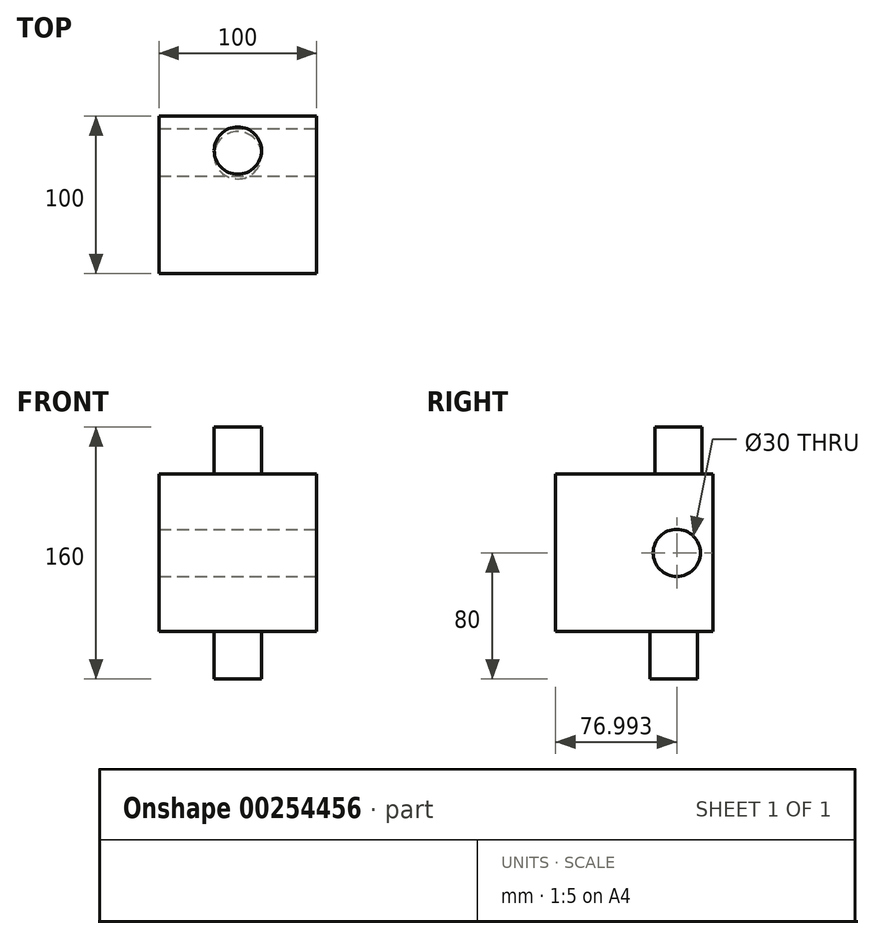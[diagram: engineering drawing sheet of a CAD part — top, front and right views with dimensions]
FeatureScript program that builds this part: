
annotation { "Feature Type Name" : "Feature", "Feature Type Description" : "" }
export const myFeature = defineFeature(function(context is Context, id is Id, definition is map)
    precondition{}
    {
        {
            var Q0;
            Q0=qCreatedBy(makeId("Front.planeOp"),FACE);
            var sketch = newSketch(context, id + "F0", { "sketchPlane" : qUnion([Q0])});
            skLineSegment(sketch, "E0.bottom", {"start": v(-50, 50) * mm, "end": v(50, 50) * mm});
            skLineSegment(sketch, "E0.top", {"start": v(-50, -50) * mm, "end": v(50, -50) * mm});
            skLineSegment(sketch, "E0.left", {"start": v(-50, 50) * mm, "end": v(-50, -50) * mm});
            skLineSegment(sketch, "E0.right", {"start": v(50, 50) * mm, "end": v(50, -50) * mm});
            skPoint(sketch, "E0.middle", {"position": v(0, 0) * mm});
            skSolve(sketch);
        }
        {
            var Q0;
            Q0 = qSketchRegion(id + "F0", true);
            extrude(context, id + "F1", {"entities" : qUnion([Q0]), "depth" : 100 * mm});
        }
        {
            var Q0;
            Q0=makeQuery(id+"F1.opExtrude","SWEPT_FACE",FACE,{"disambiguationData":[OSD([sQuery(id+"F0.wireOp",EDGE,"E0.bottom")])]});
            var sketch = newSketch(context, id + "F2", { "sketchPlane" : qUnion([Q0])});
            skCircle(sketch, "E1", {"center": v(0, -21.94) * mm, "radius": 15 * mm});
            skSolve(sketch);
        }
        {
            var Q0;
            Q0 = qSketchRegion(id + "F2", true);
            extrude(context, id + "F3", {"entities" : qUnion([Q0]), "operationType" : NewBodyOperationType.ADD, "depth" : 30 * mm});
        }
        {
            var Q0;
            Q0=makeQuery(id+"F1.opExtrude","SWEPT_FACE",FACE,{"disambiguationData":[OSD([sQuery(id+"F0.wireOp",EDGE,"E0.top")])]});
            var sketch = newSketch(context, id + "F4", { "sketchPlane" : qUnion([Q0])});
            skCircle(sketch, "E2", {"center": v(0, 24.93) * mm, "radius": 15 * mm});
            skSolve(sketch);
        }
        {
            var Q0;
            Q0 = qSketchRegion(id + "F4", true);
            extrude(context, id + "F5", {"entities" : qUnion([Q0]), "operationType" : NewBodyOperationType.ADD, "depth" : 30 * mm});
        }
        {
            var Q0;
            Q0=makeQuery(id+"F1.opExtrude","SWEPT_FACE",FACE,{"disambiguationData":[OSD([sQuery(id+"F0.wireOp",EDGE,"E0.right")])]});
            var sketch = newSketch(context, id + "F6", { "sketchPlane" : qUnion([Q0])});
            skPoint(sketch, "E3", {"position": v(-23, 0) * mm});
            skSolve(sketch);
        }
        {
            var Q0;
            Q0=sQuery(id+"F6.wireOp",VERTEX,"E3");
            var Q1;
            Q1=makeQuery(id+"F1.opExtrude","SWEPT_BODY",BODY,{"disambiguationData":[OSD([sQuery(id+"F0.wireOp",EDGE,"E0.bottom"),sQuery(id+"F0.wireOp",EDGE,"E0.top"),sQuery(id+"F0.wireOp",EDGE,"E0.left"),sQuery(id+"F0.wireOp",EDGE,"E0.right")])]});
            hole(context, id + "F7", {"style" : HoleStyle.SIMPLE, "endStyle" : HoleEndStyle.THROUGH, "holeDiameter" : 30 * mm, "tappedDepth" : 12 * mm, "tapClearance" : 3, "locations" : qUnion([Q0]), "scope" : qUnion([Q1])});
        }
    });
